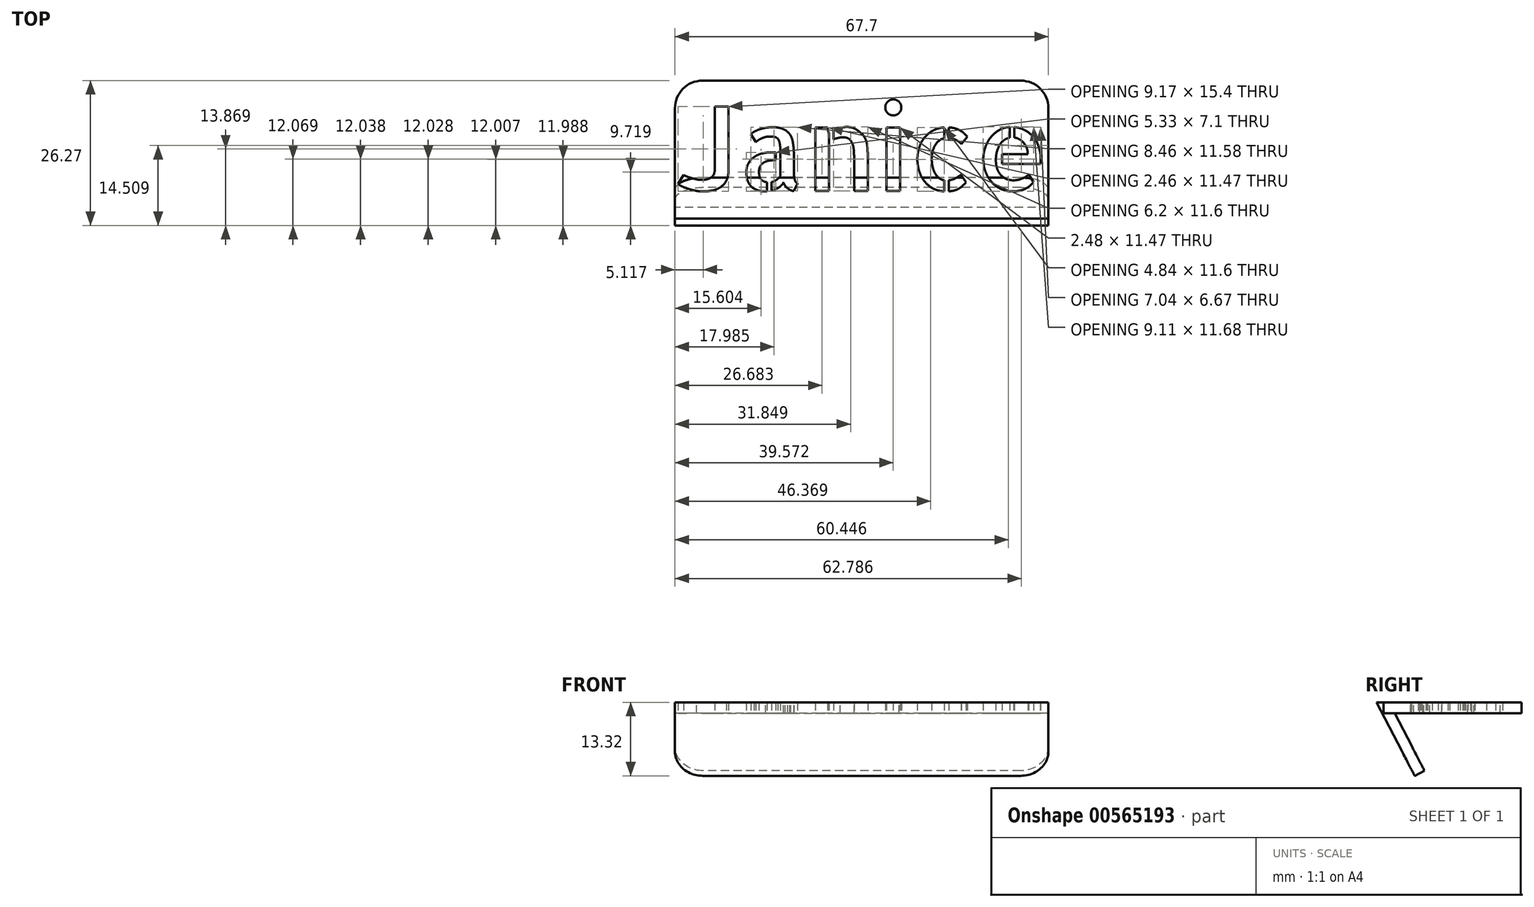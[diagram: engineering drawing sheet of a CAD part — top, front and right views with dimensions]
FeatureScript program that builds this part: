
annotation { "Feature Type Name" : "Feature", "Feature Type Description" : "" }
export const myFeature = defineFeature(function(context is Context, id is Id, definition is map)
    precondition{}
    {
        {
            var Q0;
            Q0=qCreatedBy(makeId("Top.planeOp"),FACE);
            var sketch = newSketch(context, id + "F0", { "sketchPlane" : qUnion([Q0])});
            skLineSegment(sketch, "E0.bottom", {"start": v(-23.58, 12.5) * mm, "end": v(44.12, 12.5) * mm});
            skLineSegment(sketch, "E0.top", {"start": v(-23.58, -12.5) * mm, "end": v(44.12, -12.5) * mm});
            skLineSegment(sketch, "E0.left", {"start": v(-23.58, 12.5) * mm, "end": v(-23.58, -12.5) * mm});
            skLineSegment(sketch, "E0.right", {"start": v(44.12, 12.5) * mm, "end": v(44.12, -12.5) * mm});
            skText(sketch, "E1", { "text": "Janice", "fontName": "AllertaStencil-Regular.ttf"});
            const initialGuessF0  = {"E1": [-0.02358, -0.0075, 1, 0, 0.015]};
            skSetInitialGuess(sketch, initialGuessF0);
            skSolve(sketch);
        }
        {
            var Q0;
            Q0=makeQuery(id+"F0.imprint","IMPRINT",FACE,{"disambiguationData":[TD([[makeQuery(id+"F0.imprint","IMPRINT",EDGE,{"derivedFrom":sQuery(id+"F0.wireOp",EDGE,"E0.bottom")}),-1.0]])]});
            extrude(context, id + "F1", {"entities" : qUnion([Q0]), "depth" : 2 * mm, "offsetDistance" : 25 * mm});
        }
        {
            var Q0;
            {var subQ0=sQuery(id+"F0.wireOp",EDGE,"E0.left");Q0=makeQuery(id+"FYEOEdhl7jzHk82_2.opBoolean","MERGE",FACE,{"derivedFrom":[makeQuery(id+"F1.opExtrude","SWEPT_FACE",FACE,{"disambiguationData":[OSD([subQ0])]}),makeQuery(id+"FOv1BJgTRWeWuMw_1.opExtrude","CAP_FACE",FACE,{"disambiguationData":[OSD([sQuery(id+"F0.wireOp",EDGE,"E0.bottom"),subQ0,sQuery(id+"Fjco5yBOxZZxTCI_1.wireOp",EDGE,"TpTMtmOo-qoIM-rLEy-p7IH-mKgsBanMGF23"),sQuery(id+"Fjco5yBOxZZxTCI_1.wireOp",EDGE,"Ja6BvVoQ-cpFi-Lcom-cL8s-5xC4kZiynyNl"),sQuery(id+"Fjco5yBOxZZxTCI_1.wireOp",EDGE,"utNyaJ8P-FD6r-AD7x-tpFW-fHytfVhziHLl"),sQuery(id+"Fjco5yBOxZZxTCI_1.wireOp",EDGE,"xGzW29bi-H5H8-ObLh-gdKj-mSPkAtMAUUzO")])],"isStart":true})]});}
            var sketch = newSketch(context, id + "F2", { "sketchPlane" : qUnion([Q0])});
            skLineSegment(sketch, "E2", {"start": v(11.52, 2) * mm, "end": v(5.09, -10.4) * mm});
            skLineSegment(sketch, "E3", {"start": v(5.09, -10.4) * mm, "end": v(6.87, -11.32) * mm});
            skLineSegment(sketch, "E4", {"start": v(6.87, -11.32) * mm, "end": v(13.77, 2) * mm});
            skLineSegment(sketch, "E5", {"start": v(13.77, 2) * mm, "end": v(11.52, 2) * mm});
            skSolve(sketch);
        }
        {
            var Q0;
            {var subQ4=sQuery(id+"F2.wireOp",EDGE,"E3");Q0=makeQuery(id+"F2.imprint","IMPRINT",FACE,{"disambiguationData":[TD([[makeQuery(id+"F2.imprint","IMPRINT",EDGE,{"derivedFrom":subQ4}),1.0]])]});}
            var Q1;
            Q1=makeQuery(id+"F1.opExtrude","SWEPT_FACE",FACE,{"disambiguationData":[OSD([sQuery(id+"F0.wireOp",EDGE,"E0.right")])]});
            extrude(context, id + "F3", {"entities" : qUnion([Q0]), "endBound" : BoundingType.UP_TO_SURFACE, "oppositeDirection" : true, "depth" : 75 * mm, "endBoundEntityFace" : qUnion([Q1]), "offsetDistance" : 25 * mm});
        }
        {
            var Q0;
            Q0=makeQuery(id+"F1.opExtrude","SWEPT_EDGE",EDGE,{"disambiguationData":[OSD([sQuery(id+"F0.wireOp",EDGE,"E0.bottom"),sQuery(id+"F0.wireOp",EDGE,"E0.left")])]});
            var Q1;
            Q1=makeQuery(id+"F1.opExtrude","SWEPT_EDGE",EDGE,{"disambiguationData":[OSD([sQuery(id+"F0.wireOp",EDGE,"E0.bottom"),sQuery(id+"F0.wireOp",EDGE,"E0.right")])]});
            var Q2;
            Q2=makeQuery(id+"F3.opExtrude","CAP_EDGE",EDGE,{"disambiguationData":[OSD([sQuery(id+"F2.wireOp",EDGE,"E3")])],"isStart":false});
            var Q3;
            Q3=makeQuery(id+"F3.opExtrude","CAP_EDGE",EDGE,{"disambiguationData":[OSD([sQuery(id+"F2.wireOp",EDGE,"E3")])],"isStart":true});
            var Q4;
            Q4=makeQuery(id+"F3.opExtrude","TWEAK_EDGE",EDGE,{"derivedFrom":[makeQuery(id+"F1.opExtrude","SWEPT_FACE",FACE,{"disambiguationData":[OSD([sQuery(id+"F0.wireOp",EDGE,"E0.right")])]}),makeQuery(id+"F2.imprint","IMPRINT",EDGE,{"derivedFrom":sQuery(id+"F2.wireOp",EDGE,"E3")})]});
            fillet(context, id + "F4", {"entities" : qUnion([Q0, Q1, Q2, Q3, Q4]), "radius" : 5 * mm, "tangentPropagation" : true, "allowEdgeOverflow" : false});
        }
    });
